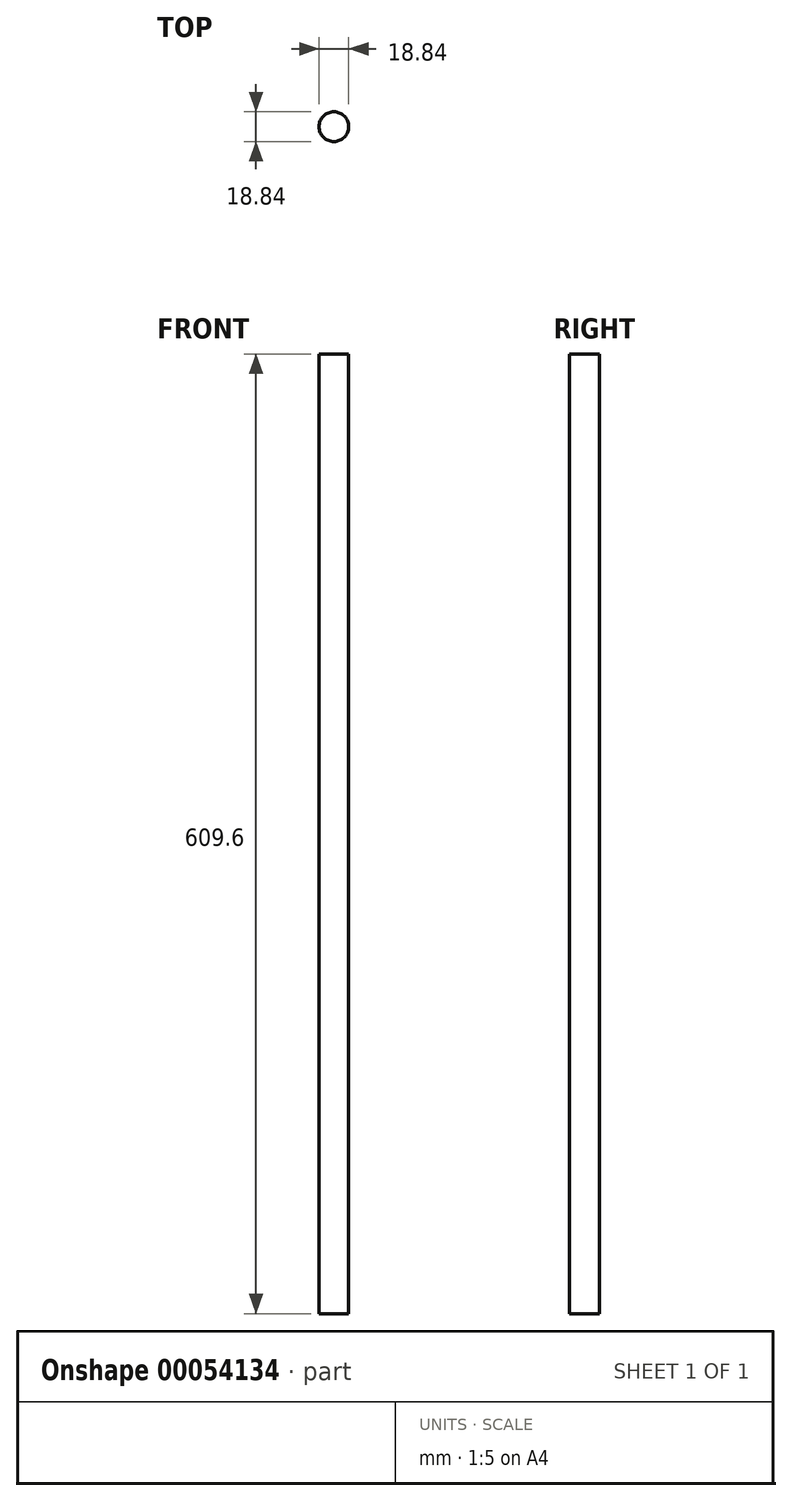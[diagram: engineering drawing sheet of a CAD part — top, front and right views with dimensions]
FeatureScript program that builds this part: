
annotation { "Feature Type Name" : "Feature", "Feature Type Description" : "" }
export const myFeature = defineFeature(function(context is Context, id is Id, definition is map)
    precondition{}
    {
        {
            var Q0;
            Q0=qCreatedBy(makeId("Top.planeOp"),FACE);
            var sketch = newSketch(context, id + "F0", { "sketchPlane" : qUnion([Q0])});
            skCircle(sketch, "E0", {"center": v(0, 0) * mm, "radius": 9.42 * mm});
            skSolve(sketch);
        }
        {
            var Q0;
            Q0 = qSketchRegion(id + "F0", true);
            extrude(context, id + "F1", {"entities" : qUnion([Q0]), "depth" : 254 * mm});
        }
        {
            var Q0;
            Q0 = qSketchRegion(id + "F0", true);
            extrude(context, id + "F2", {"entities" : qUnion([Q0]), "operationType" : NewBodyOperationType.ADD, "depth" : 609.6 * mm});
        }
        {
            var Q0;
            Q0 = qSketchRegion(id + "F0", true);
            extrude(context, id + "F3", {"entities" : qUnion([Q0]), "operationType" : NewBodyOperationType.ADD, "depth" : 609.6 * mm});
        }
    });
